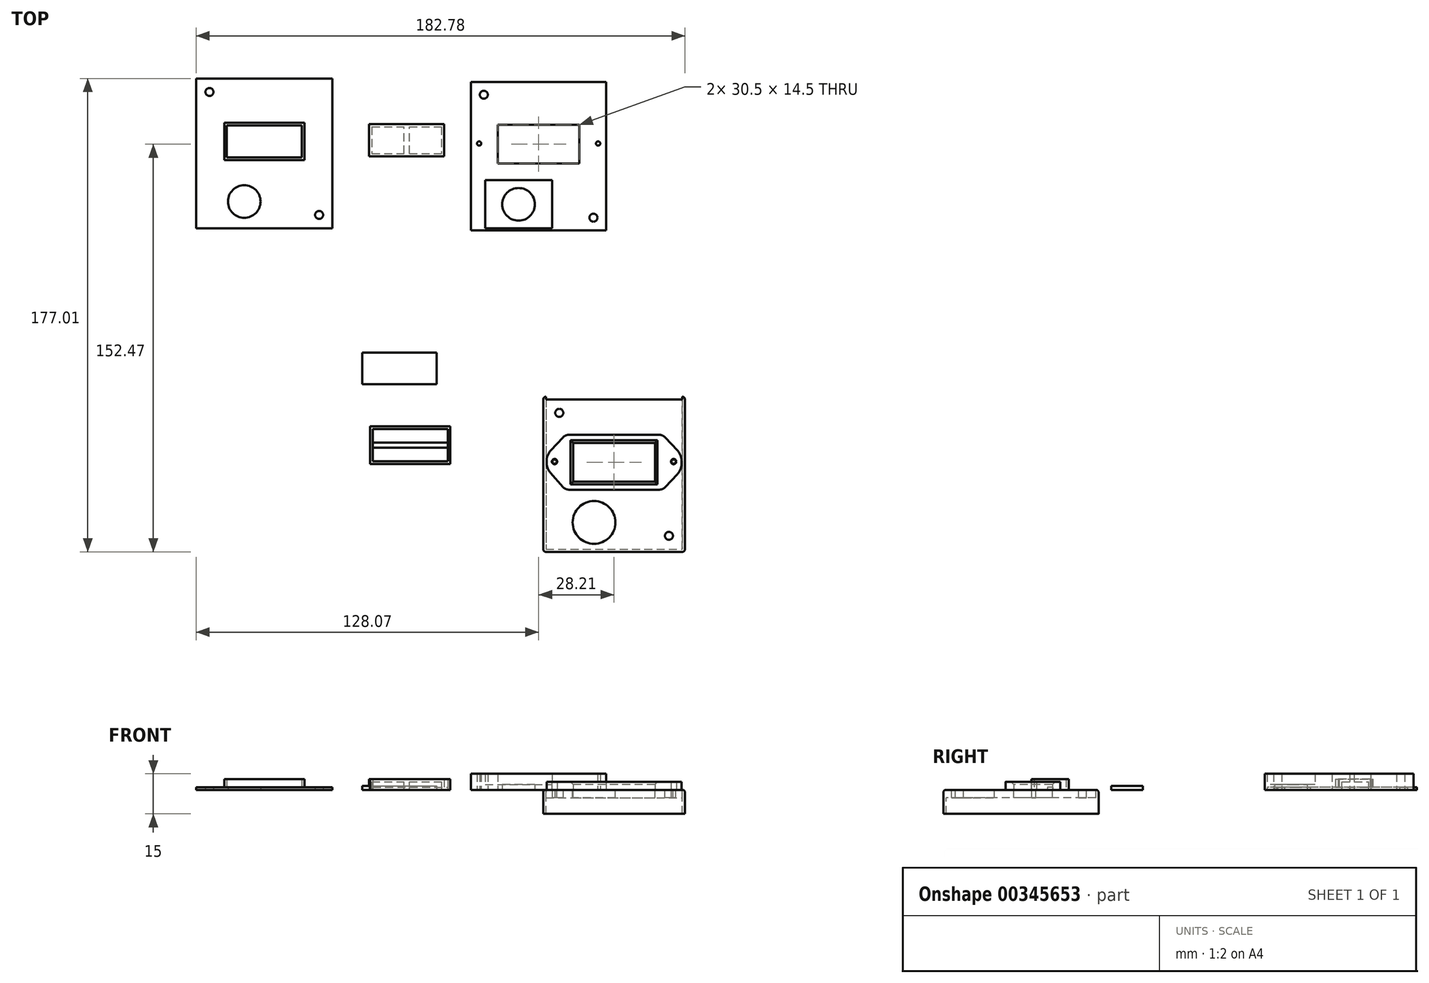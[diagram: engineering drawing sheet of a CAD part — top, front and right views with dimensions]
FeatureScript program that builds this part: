
annotation { "Feature Type Name" : "Feature", "Feature Type Description" : "" }
export const myFeature = defineFeature(function(context is Context, id is Id, definition is map)
    precondition{}
    {
        {
            var Q0;
            Q0=qCreatedBy(makeId("Top.planeOp"),FACE);
            var sketch = newSketch(context, id + "F0", { "sketchPlane" : qUnion([Q0])});
            skLineSegment(sketch, "E0.bottom", {"start": v(25.5, 28) * mm, "end": v(-25.5, 28) * mm});
            skLineSegment(sketch, "E0.top", {"start": v(25.5, -28) * mm, "end": v(-25.5, -28) * mm});
            skLineSegment(sketch, "E0.left", {"start": v(25.5, 28) * mm, "end": v(25.5, -28) * mm});
            skLineSegment(sketch, "E0.right", {"start": v(-25.5, 28) * mm, "end": v(-25.5, -28) * mm});
            skCircle(sketch, "E1", {"center": v(-20.5, 23) * mm, "radius": 1.5 * mm});
            skCircle(sketch, "E2", {"center": v(20.5, -23) * mm, "radius": 1.5 * mm});
            skCircle(sketch, "E3", {"center": v(-7.5, -18) * mm, "radius": 6.1 * mm});
            skLineSegment(sketch, "E4.bottom", {"start": v(-15.25, 11.75) * mm, "end": v(15.25, 11.75) * mm});
            skLineSegment(sketch, "E4.top", {"start": v(-15.25, -2.75) * mm, "end": v(15.25, -2.75) * mm});
            skLineSegment(sketch, "E4.left", {"start": v(-15.25, 11.75) * mm, "end": v(-15.25, -2.75) * mm});
            skLineSegment(sketch, "E4.right", {"start": v(15.25, 11.75) * mm, "end": v(15.25, -2.75) * mm});
            skPoint(sketch, "E5.middle", {"position": v(-103.8, -4.8) * mm});
            skLineSegment(sketch, "E6.bottom", {"start": v(-116.57, 11.54) * mm, "end": v(-88.57, 11.54) * mm});
            skLineSegment(sketch, "E6.top", {"start": v(-116.57, -0.46) * mm, "end": v(-88.57, -0.46) * mm});
            skLineSegment(sketch, "E6.left", {"start": v(-116.57, 11.54) * mm, "end": v(-116.57, -0.46) * mm});
            skLineSegment(sketch, "E6.right", {"start": v(-88.57, 11.54) * mm, "end": v(-88.57, -0.46) * mm});
            skLineSegment(sketch, "E7.bottom", {"start": v(-112.82, 11.54) * mm, "end": v(-110.32, 11.54) * mm});
            skLineSegment(sketch, "E7.top", {"start": v(-112.82, -0.46) * mm, "end": v(-110.32, -0.46) * mm});
            skLineSegment(sketch, "E7.left", {"start": v(-112.82, 11.54) * mm, "end": v(-112.82, -0.46) * mm});
            skLineSegment(sketch, "E7.right", {"start": v(-110.32, 11.54) * mm, "end": v(-110.32, -0.46) * mm});
            skLineSegment(sketch, "E8.bottom", {"start": v(-94.82, 11.54) * mm, "end": v(-92.32, 11.54) * mm});
            skLineSegment(sketch, "E8.top", {"start": v(-94.82, -0.46) * mm, "end": v(-92.32, -0.46) * mm});
            skLineSegment(sketch, "E8.left", {"start": v(-94.82, 11.54) * mm, "end": v(-94.82, -0.46) * mm});
            skLineSegment(sketch, "E8.right", {"start": v(-92.32, 11.54) * mm, "end": v(-92.32, -0.46) * mm});
            skLineSegment(sketch, "E9.bottom", {"start": v(-114.57, 8.54) * mm, "end": v(-108.57, 8.54) * mm, "construction": true});
            skLineSegment(sketch, "E9.top", {"start": v(-114.57, 2.54) * mm, "end": v(-108.57, 2.54) * mm, "construction": true});
            skLineSegment(sketch, "E9.left", {"start": v(-114.57, 8.54) * mm, "end": v(-114.57, 2.54) * mm, "construction": true});
            skLineSegment(sketch, "E9.right", {"start": v(-108.57, 8.54) * mm, "end": v(-108.57, 2.54) * mm, "construction": true});
            skLineSegment(sketch, "E10.bottom", {"start": v(-96.57, 8.54) * mm, "end": v(-90.57, 8.54) * mm, "construction": true});
            skLineSegment(sketch, "E10.top", {"start": v(-96.57, 2.54) * mm, "end": v(-90.57, 2.54) * mm, "construction": true});
            skLineSegment(sketch, "E10.left", {"start": v(-96.57, 8.54) * mm, "end": v(-96.57, 2.54) * mm, "construction": true});
            skLineSegment(sketch, "E10.right", {"start": v(-90.57, 8.54) * mm, "end": v(-90.57, 2.54) * mm, "construction": true});
            skLineSegment(sketch, "E11.bottom", {"start": v(-2.5, 11.75) * mm, "end": v(2.5, 11.75) * mm});
            skLineSegment(sketch, "E11.top", {"start": v(-2.5, -2.75) * mm, "end": v(2.5, -2.75) * mm});
            skLineSegment(sketch, "E11.left", {"start": v(-2.5, 11.75) * mm, "end": v(-2.5, -2.75) * mm});
            skLineSegment(sketch, "E11.right", {"start": v(2.5, 11.75) * mm, "end": v(2.5, -2.75) * mm});
            skLineSegment(sketch, "E12.bottom", {"start": v(-6.25, 10.5) * mm, "end": v(5.75, 10.5) * mm, "construction": true});
            skLineSegment(sketch, "E12.top", {"start": v(-6.25, -1.5) * mm, "end": v(5.75, -1.5) * mm, "construction": true});
            skLineSegment(sketch, "E12.left", {"start": v(-6.25, 10.5) * mm, "end": v(-6.25, -1.5) * mm, "construction": true});
            skLineSegment(sketch, "E12.right", {"start": v(5.75, 10.5) * mm, "end": v(5.75, -1.5) * mm, "construction": true});
            skLineSegment(sketch, "E13.bottom", {"start": v(-128.07, 29.04) * mm, "end": v(-77.07, 29.04) * mm});
            skLineSegment(sketch, "E13.top", {"start": v(-128.07, -26.96) * mm, "end": v(-77.07, -26.96) * mm});
            skLineSegment(sketch, "E13.left", {"start": v(-128.07, 29.04) * mm, "end": v(-128.07, -26.96) * mm});
            skLineSegment(sketch, "E13.right", {"start": v(-77.07, 29.04) * mm, "end": v(-77.07, -26.96) * mm});
            skCircle(sketch, "E14", {"center": v(-123.07, 24.04) * mm, "radius": 1.5 * mm});
            skCircle(sketch, "E15", {"center": v(-82.07, -21.96) * mm, "radius": 1.5 * mm});
            skLineSegment(sketch, "E16.bottom", {"start": v(-14, 10.5) * mm, "end": v(14, 10.5) * mm, "construction": true});
            skLineSegment(sketch, "E16.top", {"start": v(-14, -1.5) * mm, "end": v(14, -1.5) * mm, "construction": true});
            skLineSegment(sketch, "E16.left", {"start": v(-14, 10.5) * mm, "end": v(-14, -1.5) * mm, "construction": true});
            skLineSegment(sketch, "E16.right", {"start": v(14, 10.5) * mm, "end": v(14, -1.5) * mm, "construction": true});
            skCircle(sketch, "E17", {"center": v(-110.07, -16.96) * mm, "radius": 6.1 * mm});
            skSolve(sketch);
        }
        {
            var Q0;
            Q0=makeQuery(id+"F0.imprint","IMPRINT",FACE,{"disambiguationData":[TD([[makeQuery(id+"F0.imprint","IMPRINT",EDGE,{"derivedFrom":sQuery(id+"F0.wireOp",EDGE,"E0.bottom")}),1.0]])]});
            var Q1;
            Q1=makeQuery(id+"F0.imprint","IMPRINT",FACE,{"disambiguationData":[TD([[makeQuery(id+"F0.imprint","IMPRINT",EDGE,{"derivedFrom":sQuery(id+"F0.wireOp",EDGE,"LN2d2Qam-zQ4N-hJWI-jsZm-hQ2YjQqxJFMe.bottom")}),-1.0]])]});
            var Q2;
            Q2=makeQuery(id+"F0.imprint","IMPRINT",FACE,{"disambiguationData":[TD([[makeQuery(id+"F0.imprint","IMPRINT",EDGE,{"derivedFrom":sQuery(id+"F0.wireOp",EDGE,"Tyq8l7xN-NJ6r-rAiC-5Q4v-MCzvgNdMf9WX.bottom")}),-1.0]])]});
            var Q3;
            Q3=makeQuery(id+"F0.imprint","IMPRINT",FACE,{"disambiguationData":[TD([[makeQuery(id+"F0.imprint","IMPRINT",EDGE,{"derivedFrom":sQuery(id+"F0.wireOp",EDGE,"E11.bottom")}),-1.0]])]});
            var Q4;
            {var subQ12=sQuery(id+"F0.wireOp",EDGE,"E6.left");Q4=makeQuery(id+"F0.imprint","IMPRINT",FACE,{"disambiguationData":[TD([[makeQuery(id+"F0.imprint","IMPRINT",EDGE,{"derivedFrom":subQ12}),-1.0]])]});}
            var Q5;
            Q5=makeQuery(id+"F0.imprint","IMPRINT",FACE,{"disambiguationData":[TD([[makeQuery(id+"F0.imprint","IMPRINT",EDGE,{"derivedFrom":sQuery(id+"F0.wireOp",EDGE,"E7.bottom")}),-1.0]])]});
            var Q6;
            Q6=makeQuery(id+"F0.imprint","IMPRINT",FACE,{"disambiguationData":[TD([[makeQuery(id+"F0.imprint","IMPRINT",EDGE,{"derivedFrom":sQuery(id+"F0.wireOp",EDGE,"E8.bottom")}),-1.0]])]});
            var Q7;
            Q7=makeQuery(id+"F0.imprint","IMPRINT",FACE,{"disambiguationData":[TD([[makeQuery(id+"F0.imprint","IMPRINT",EDGE,{"derivedFrom":sQuery(id+"F0.wireOp",EDGE,"V3zyF6Pa-9TGi-MSfi-dUwD-Oto6uP0OLka4.bottom")}),-1.0]])]});
            extrude(context, id + "F1", {"entities" : qUnion([Q0, Q1, Q2, Q3, Q4, Q5, Q6, Q7]), "depth" : 1 * mm});
        }
        {
            var Q0;
            Q0=qCreatedBy(makeId("Top.planeOp"),FACE);
            var sketch = newSketch(context, id + "F2", { "sketchPlane" : qUnion([Q0])});
            skPoint(sketch, "E18.middle", {"position": v(28.78, -122.02) * mm});
            skLineSegment(sketch, "E19.bottom", {"start": v(14.21, -108.47) * mm, "end": v(42.21, -108.47) * mm, "construction": true});
            skLineSegment(sketch, "E19.top", {"start": v(14.21, -120.47) * mm, "end": v(42.21, -120.47) * mm, "construction": true});
            skLineSegment(sketch, "E19.left", {"start": v(14.21, -108.47) * mm, "end": v(14.21, -120.47) * mm, "construction": true});
            skLineSegment(sketch, "E19.right", {"start": v(42.21, -108.47) * mm, "end": v(42.21, -120.47) * mm, "construction": true});
            skLineSegment(sketch, "E20.bottom", {"start": v(20.96, -108.47) * mm, "end": v(23.46, -108.47) * mm, "construction": true});
            skLineSegment(sketch, "E20.top", {"start": v(20.96, -120.47) * mm, "end": v(23.46, -120.47) * mm, "construction": true});
            skLineSegment(sketch, "E20.left", {"start": v(20.96, -108.47) * mm, "end": v(20.96, -120.47) * mm, "construction": true});
            skLineSegment(sketch, "E20.right", {"start": v(23.46, -108.47) * mm, "end": v(23.46, -120.47) * mm, "construction": true});
            skLineSegment(sketch, "E21.bottom", {"start": v(32.96, -108.47) * mm, "end": v(35.46, -108.47) * mm, "construction": true});
            skLineSegment(sketch, "E21.top", {"start": v(32.96, -120.47) * mm, "end": v(35.46, -120.47) * mm, "construction": true});
            skLineSegment(sketch, "E21.left", {"start": v(32.96, -108.47) * mm, "end": v(32.96, -120.47) * mm, "construction": true});
            skLineSegment(sketch, "E21.right", {"start": v(35.46, -108.47) * mm, "end": v(35.46, -120.47) * mm, "construction": true});
            skLineSegment(sketch, "E22.bottom", {"start": v(19.21, -111.47) * mm, "end": v(25.21, -111.47) * mm, "construction": true});
            skLineSegment(sketch, "E22.top", {"start": v(19.21, -117.47) * mm, "end": v(25.21, -117.47) * mm, "construction": true});
            skLineSegment(sketch, "E22.left", {"start": v(19.21, -111.47) * mm, "end": v(19.21, -117.47) * mm, "construction": true});
            skLineSegment(sketch, "E22.right", {"start": v(25.21, -111.47) * mm, "end": v(25.21, -117.47) * mm, "construction": true});
            skLineSegment(sketch, "E23.bottom", {"start": v(31.21, -111.47) * mm, "end": v(37.21, -111.47) * mm, "construction": true});
            skLineSegment(sketch, "E23.top", {"start": v(31.21, -117.47) * mm, "end": v(37.21, -117.47) * mm, "construction": true});
            skLineSegment(sketch, "E23.left", {"start": v(31.21, -111.47) * mm, "end": v(31.21, -117.47) * mm, "construction": true});
            skLineSegment(sketch, "E23.right", {"start": v(37.21, -111.47) * mm, "end": v(37.21, -117.47) * mm, "construction": true});
            skLineSegment(sketch, "E24.bottom", {"start": v(2.71, -90.97) * mm, "end": v(53.71, -90.97) * mm});
            skLineSegment(sketch, "E24.top", {"start": v(2.71, -146.97) * mm, "end": v(53.71, -146.97) * mm});
            skLineSegment(sketch, "E24.left", {"start": v(2.71, -90.97) * mm, "end": v(2.71, -146.97) * mm});
            skLineSegment(sketch, "E24.right", {"start": v(53.71, -90.97) * mm, "end": v(53.71, -146.97) * mm});
            skCircle(sketch, "E25", {"center": v(7.71, -95.97) * mm, "radius": 1.5 * mm});
            skCircle(sketch, "E26", {"center": v(48.71, -141.97) * mm, "radius": 1.5 * mm});
            skCircle(sketch, "E27", {"center": v(20.71, -136.97) * mm, "radius": 8 * mm});
            skLineSegment(sketch, "E28.bottom", {"start": v(12.96, -107.22) * mm, "end": v(43.46, -107.22) * mm});
            skLineSegment(sketch, "E28.top", {"start": v(12.96, -121.72) * mm, "end": v(43.46, -121.72) * mm});
            skLineSegment(sketch, "E28.left", {"start": v(12.96, -107.22) * mm, "end": v(12.96, -121.72) * mm});
            skLineSegment(sketch, "E28.right", {"start": v(43.46, -107.22) * mm, "end": v(43.46, -121.72) * mm});
            skPoint(sketch, "E29.middle", {"position": v(-49.22, -118.43) * mm});
            skLineSegment(sketch, "E30.bottom", {"start": v(-62, -102.08) * mm, "end": v(-34, -102.08) * mm});
            skLineSegment(sketch, "E30.top", {"start": v(-62, -114.08) * mm, "end": v(-34, -114.08) * mm});
            skLineSegment(sketch, "E30.left", {"start": v(-62, -102.08) * mm, "end": v(-62, -114.08) * mm});
            skLineSegment(sketch, "E30.right", {"start": v(-34, -102.08) * mm, "end": v(-34, -114.08) * mm});
            skLineSegment(sketch, "E31.bottom", {"start": v(-57.25, -102.08) * mm, "end": v(-54.75, -102.08) * mm, "construction": true});
            skLineSegment(sketch, "E31.top", {"start": v(-57.25, -114.08) * mm, "end": v(-54.75, -114.08) * mm, "construction": true});
            skLineSegment(sketch, "E31.left", {"start": v(-57.25, -102.08) * mm, "end": v(-57.25, -114.08) * mm, "construction": true});
            skLineSegment(sketch, "E31.right", {"start": v(-54.75, -102.08) * mm, "end": v(-54.75, -114.08) * mm, "construction": true});
            skLineSegment(sketch, "E32.bottom", {"start": v(-41.25, -102.08) * mm, "end": v(-38.75, -102.08) * mm, "construction": true});
            skLineSegment(sketch, "E32.top", {"start": v(-41.25, -114.08) * mm, "end": v(-38.75, -114.08) * mm, "construction": true});
            skLineSegment(sketch, "E32.left", {"start": v(-41.25, -102.08) * mm, "end": v(-41.25, -114.08) * mm, "construction": true});
            skLineSegment(sketch, "E32.right", {"start": v(-38.75, -102.08) * mm, "end": v(-38.75, -114.08) * mm, "construction": true});
            skLineSegment(sketch, "E33.bottom", {"start": v(-59, -105.08) * mm, "end": v(-53, -105.08) * mm, "construction": true});
            skLineSegment(sketch, "E33.top", {"start": v(-59, -111.08) * mm, "end": v(-53, -111.08) * mm, "construction": true});
            skLineSegment(sketch, "E33.left", {"start": v(-59, -105.08) * mm, "end": v(-59, -111.08) * mm, "construction": true});
            skLineSegment(sketch, "E33.right", {"start": v(-53, -105.08) * mm, "end": v(-53, -111.08) * mm, "construction": true});
            skLineSegment(sketch, "E34.bottom", {"start": v(-43, -105.08) * mm, "end": v(-37, -105.08) * mm, "construction": true});
            skLineSegment(sketch, "E34.top", {"start": v(-43, -111.08) * mm, "end": v(-37, -111.08) * mm, "construction": true});
            skLineSegment(sketch, "E34.left", {"start": v(-43, -105.08) * mm, "end": v(-43, -111.08) * mm, "construction": true});
            skLineSegment(sketch, "E34.right", {"start": v(-37, -105.08) * mm, "end": v(-37, -111.08) * mm, "construction": true});
            skLineSegment(sketch, "E35.bottom", {"start": v(-63, -101.08) * mm, "end": v(-33, -101.08) * mm});
            skLineSegment(sketch, "E35.top", {"start": v(-63, -115.08) * mm, "end": v(-33, -115.08) * mm});
            skLineSegment(sketch, "E35.left", {"start": v(-63, -101.08) * mm, "end": v(-63, -115.08) * mm});
            skLineSegment(sketch, "E35.right", {"start": v(-33, -101.08) * mm, "end": v(-33, -115.08) * mm});
            skLineSegment(sketch, "E36.bottom", {"start": v(-62, -107.08) * mm, "end": v(-34, -107.08) * mm});
            skLineSegment(sketch, "E36.top", {"start": v(-62, -109.08) * mm, "end": v(-34, -109.08) * mm});
            skLineSegment(sketch, "E36.left", {"start": v(-62, -107.08) * mm, "end": v(-62, -109.08) * mm});
            skLineSegment(sketch, "E36.right", {"start": v(-34, -107.08) * mm, "end": v(-34, -109.08) * mm});
            skLineSegment(sketch, "E37.bottom", {"start": v(-53, -102.08) * mm, "end": v(-43, -102.08) * mm});
            skLineSegment(sketch, "E37.top", {"start": v(-53, -114.08) * mm, "end": v(-43, -114.08) * mm});
            skLineSegment(sketch, "E37.left", {"start": v(-53, -102.08) * mm, "end": v(-53, -114.08) * mm});
            skLineSegment(sketch, "E37.right", {"start": v(-43, -102.08) * mm, "end": v(-43, -114.08) * mm});
            skLineSegment(sketch, "E38.top", {"start": v(2.71, -89.97) * mm, "end": v(53.71, -89.97) * mm});
            skLineSegment(sketch, "E38.left", {"start": v(2.71, -90.97) * mm, "end": v(2.71, -89.97) * mm});
            skLineSegment(sketch, "E38.right", {"start": v(53.71, -90.97) * mm, "end": v(53.71, -89.97) * mm});
            skLineSegment(sketch, "E39.top", {"start": v(2.71, -147.97) * mm, "end": v(53.71, -147.97) * mm});
            skLineSegment(sketch, "E39.left", {"start": v(2.71, -146.97) * mm, "end": v(2.71, -147.97) * mm});
            skLineSegment(sketch, "E39.right", {"start": v(53.71, -146.97) * mm, "end": v(53.71, -147.97) * mm});
            skLineSegment(sketch, "E40.bottom", {"start": v(53.71, -89.97) * mm, "end": v(54.71, -89.97) * mm});
            skLineSegment(sketch, "E40.top", {"start": v(53.71, -147.97) * mm, "end": v(54.71, -147.97) * mm});
            skLineSegment(sketch, "E40.left", {"start": v(53.71, -89.97) * mm, "end": v(53.71, -147.97) * mm});
            skLineSegment(sketch, "E40.right", {"start": v(54.71, -89.97) * mm, "end": v(54.71, -147.97) * mm});
            skLineSegment(sketch, "E41.bottom", {"start": v(2.71, -89.97) * mm, "end": v(1.71, -89.97) * mm});
            skLineSegment(sketch, "E41.top", {"start": v(2.71, -147.97) * mm, "end": v(1.71, -147.97) * mm});
            skLineSegment(sketch, "E41.left", {"start": v(2.71, -89.97) * mm, "end": v(2.71, -147.97) * mm});
            skLineSegment(sketch, "E41.right", {"start": v(1.71, -89.97) * mm, "end": v(1.71, -147.97) * mm});
            skCircle(sketch, "E42", {"center": v(5.96, -114.22) * mm, "radius": 0.8 * mm});
            skCircle(sketch, "E43", {"center": v(50.46, -114.22) * mm, "radius": 0.8 * mm});
            skSolve(sketch);
        }
        {
            var Q0;
            Q0=makeQuery(id+"F1.opExtrude","CAP_FACE",FACE,{"disambiguationData":[OSD([sQuery(id+"F0.wireOp",EDGE,"E6.bottom"),sQuery(id+"F0.wireOp",EDGE,"E6.top"),sQuery(id+"F0.wireOp",EDGE,"E6.left"),sQuery(id+"F0.wireOp",EDGE,"E6.right"),sQuery(id+"F0.wireOp",EDGE,"E7.left"),sQuery(id+"F0.wireOp",EDGE,"E7.right"),sQuery(id+"F0.wireOp",EDGE,"E8.left"),sQuery(id+"F0.wireOp",EDGE,"E8.right"),sQuery(id+"F0.wireOp",EDGE,"E13.bottom"),sQuery(id+"F0.wireOp",EDGE,"E13.top"),sQuery(id+"F0.wireOp",EDGE,"E13.left"),sQuery(id+"F0.wireOp",EDGE,"E13.right"),sQuery(id+"F0.wireOp",EDGE,"E14"),sQuery(id+"F0.wireOp",EDGE,"E15"),sQuery(id+"F0.wireOp",EDGE,"E17"),sQuery(id+"F0.wireOp",EDGE,"V3zyF6Pa-9TGi-MSfi-dUwD-Oto6uP0OLka4.left"),sQuery(id+"F0.wireOp",EDGE,"V3zyF6Pa-9TGi-MSfi-dUwD-Oto6uP0OLka4.right")])],"isStart":false});
            var sketch = newSketch(context, id + "F3", { "sketchPlane" : qUnion([Q0])});
            skLineSegment(sketch, "E44.bottom", {"start": v(-116.57, 11.54) * mm, "end": v(-88.57, 11.54) * mm});
            skLineSegment(sketch, "E44.top", {"start": v(-116.57, 12.54) * mm, "end": v(-88.57, 12.54) * mm});
            skLineSegment(sketch, "E44.left", {"start": v(-116.57, 11.54) * mm, "end": v(-116.57, 12.54) * mm});
            skLineSegment(sketch, "E44.right", {"start": v(-88.57, 11.54) * mm, "end": v(-88.57, 12.54) * mm});
            skLineSegment(sketch, "E45.bottom", {"start": v(-116.57, -0.46) * mm, "end": v(-88.57, -0.46) * mm});
            skLineSegment(sketch, "E45.top", {"start": v(-116.57, -1.46) * mm, "end": v(-88.57, -1.46) * mm});
            skLineSegment(sketch, "E45.left", {"start": v(-116.57, -0.46) * mm, "end": v(-116.57, -1.46) * mm});
            skLineSegment(sketch, "E45.right", {"start": v(-88.57, -0.46) * mm, "end": v(-88.57, -1.46) * mm});
            skLineSegment(sketch, "E46.bottom", {"start": v(-116.57, -1.46) * mm, "end": v(-117.57, -1.46) * mm});
            skLineSegment(sketch, "E46.top", {"start": v(-116.57, 12.54) * mm, "end": v(-117.57, 12.54) * mm});
            skLineSegment(sketch, "E46.left", {"start": v(-116.57, -1.46) * mm, "end": v(-116.57, 12.54) * mm});
            skLineSegment(sketch, "E46.right", {"start": v(-117.57, -1.46) * mm, "end": v(-117.57, 12.54) * mm});
            skLineSegment(sketch, "E47.bottom", {"start": v(-88.57, 12.54) * mm, "end": v(-87.57, 12.54) * mm});
            skLineSegment(sketch, "E47.top", {"start": v(-88.57, -1.46) * mm, "end": v(-87.57, -1.46) * mm});
            skLineSegment(sketch, "E47.left", {"start": v(-88.57, 12.54) * mm, "end": v(-88.57, -1.46) * mm});
            skLineSegment(sketch, "E47.right", {"start": v(-87.57, 12.54) * mm, "end": v(-87.57, -1.46) * mm});
            skSolve(sketch);
        }
        {
            var Q0;
            Q0 = qSketchRegion(id + "F3", true);
            extrude(context, id + "F4", {"entities" : qUnion([Q0]), "operationType" : NewBodyOperationType.ADD, "depth" : 3 * mm});
        }
        {
            var Q0;
            Q0=qCreatedBy(makeId("Top.planeOp"),FACE);
            var sketch = newSketch(context, id + "F5", { "sketchPlane" : qUnion([Q0])});
            skLineSegment(sketch, "E48.bottom", {"start": v(-63.36, 12) * mm, "end": v(-35.36, 12) * mm});
            skLineSegment(sketch, "E48.top", {"start": v(-63.36, 0) * mm, "end": v(-35.36, 0) * mm});
            skLineSegment(sketch, "E48.left", {"start": v(-63.36, 12) * mm, "end": v(-63.36, 0) * mm});
            skLineSegment(sketch, "E48.right", {"start": v(-35.36, 12) * mm, "end": v(-35.36, 0) * mm});
            skLineSegment(sketch, "E49.bottom", {"start": v(-65.94, -73.47) * mm, "end": v(-38.14, -73.47) * mm});
            skLineSegment(sketch, "E49.top", {"start": v(-65.94, -85.27) * mm, "end": v(-38.14, -85.27) * mm});
            skLineSegment(sketch, "E49.left", {"start": v(-65.94, -73.47) * mm, "end": v(-65.94, -85.27) * mm});
            skLineSegment(sketch, "E49.right", {"start": v(-38.14, -73.47) * mm, "end": v(-38.14, -85.27) * mm});
            skSolve(sketch);
        }
        {
            var Q0;
            Q0=makeQuery(id+"F5.imprint","IMPRINT",FACE,{"disambiguationData":[TD([[makeQuery(id+"F5.imprint","IMPRINT",EDGE,{"derivedFrom":sQuery(id+"F5.wireOp",EDGE,"E48.bottom")}),-1.0]])]});
            extrude(context, id + "F6", {"entities" : qUnion([Q0]), "depth" : 4 * mm});
        }
        {
            var Q0;
            Q0=makeQuery(id+"F6.opExtrude","CAP_FACE",FACE,{"disambiguationData":[OSD([sQuery(id+"F5.wireOp",EDGE,"E48.bottom"),sQuery(id+"F5.wireOp",EDGE,"E48.top"),sQuery(id+"F5.wireOp",EDGE,"E48.left"),sQuery(id+"F5.wireOp",EDGE,"E48.right")])],"isStart":true});
            shell(context, id + "F7", {"entities" : qUnion([Q0]), "thickness" : 1 * mm});
        }
        {
            var Q0;
            Q0=makeQuery(id+"F7.opShell","OFFSET_FACE",FACE,{"disambiguationData":[OSD([sQuery(id+"F5.wireOp",EDGE,"E48.bottom"),sQuery(id+"F5.wireOp",EDGE,"E48.top"),sQuery(id+"F5.wireOp",EDGE,"E48.left"),sQuery(id+"F5.wireOp",EDGE,"E48.right")])]});
            var sketch = newSketch(context, id + "F8", { "sketchPlane" : qUnion([Q0])});
            skLineSegment(sketch, "E50.bottom", {"start": v(-50.36, -1) * mm, "end": v(-48.36, -1) * mm});
            skLineSegment(sketch, "E50.top", {"start": v(-50.36, -11) * mm, "end": v(-48.36, -11) * mm});
            skLineSegment(sketch, "E50.left", {"start": v(-50.36, -1) * mm, "end": v(-50.36, -11) * mm});
            skLineSegment(sketch, "E50.right", {"start": v(-48.36, -1) * mm, "end": v(-48.36, -11) * mm});
            skSolve(sketch);
        }
        {
            var Q0;
            Q0=makeQuery(id+"F8.imprint","IMPRINT",FACE,{"disambiguationData":[TD([[makeQuery(id+"F8.imprint","IMPRINT",EDGE,{"derivedFrom":sQuery(id+"F8.wireOp",EDGE,"E50.bottom")}),-1.0]])]});
            extrude(context, id + "F9", {"entities" : qUnion([Q0]), "operationType" : NewBodyOperationType.ADD, "depth" : 3 * mm});
        }
        {
            var Q0;
            Q0=makeQuery(id+"F1.opExtrude","CAP_FACE",FACE,{"disambiguationData":[OSD([sQuery(id+"F0.wireOp",EDGE,"E0.bottom"),sQuery(id+"F0.wireOp",EDGE,"E0.top"),sQuery(id+"F0.wireOp",EDGE,"E0.left"),sQuery(id+"F0.wireOp",EDGE,"E0.right"),sQuery(id+"F0.wireOp",EDGE,"E1"),sQuery(id+"F0.wireOp",EDGE,"E2"),sQuery(id+"F0.wireOp",EDGE,"E3"),sQuery(id+"F0.wireOp",EDGE,"E4.bottom"),sQuery(id+"F0.wireOp",EDGE,"E4.top"),sQuery(id+"F0.wireOp",EDGE,"E4.left"),sQuery(id+"F0.wireOp",EDGE,"E4.right"),sQuery(id+"F0.wireOp",EDGE,"E11.left"),sQuery(id+"F0.wireOp",EDGE,"E11.right")])],"isStart":false});
            var sketch = newSketch(context, id + "F10", { "sketchPlane" : qUnion([Q0])});
            skLineSegment(sketch, "E51.bottom", {"start": v(-6.25, 10.25) * mm, "end": v(5.75, 10.25) * mm, "construction": true});
            skLineSegment(sketch, "E51.top", {"start": v(-6.25, -1.75) * mm, "end": v(5.75, -1.75) * mm, "construction": true});
            skLineSegment(sketch, "E51.left", {"start": v(-6.25, 10.25) * mm, "end": v(-6.25, -1.75) * mm, "construction": true});
            skLineSegment(sketch, "E51.right", {"start": v(5.75, 10.25) * mm, "end": v(5.75, -1.75) * mm, "construction": true});
            skSolve(sketch);
        }
        {
            var Q0;
            {var subQ3=sQuery(id+"F2.wireOp",EDGE,"E30.left");Q0=makeQuery(id+"F2.imprint","IMPRINT",FACE,{"disambiguationData":[TD([[makeQuery(id+"F2.imprint","IMPRINT",EDGE,{"derivedFrom":subQ3}),-1.0]])]});}
            extrude(context, id + "F11", {"entities" : qUnion([Q0]), "depth" : 4 * mm});
        }
        {
            var Q0;
            Q0=makeQuery(id+"F2.imprint","IMPRINT",FACE,{"disambiguationData":[TD([[makeQuery(id+"F2.imprint","IMPRINT",EDGE,{"derivedFrom":sQuery(id+"F2.wireOp",EDGE,"E25")}),-1.0]])]});
            extrude(context, id + "F12", {"entities" : qUnion([Q0]), "oppositeDirection" : true, "depth" : 3 * mm});
        }
        {
            var Q0;
            Q0=makeQuery(id+"F2.imprint","IMPRINT",FACE,{"disambiguationData":[TD([[makeQuery(id+"F2.imprint","IMPRINT",EDGE,{"derivedFrom":sQuery(id+"F2.wireOp",EDGE,"E36.bottom")}),-1.0]])]});
            var Q1;
            {var subQ5=sQuery(id+"F2.wireOp",EDGE,"E37.bottom");Q1=makeQuery(id+"F2.imprint","IMPRINT",FACE,{"disambiguationData":[TD([[makeQuery(id+"F2.imprint","IMPRINT",EDGE,{"derivedFrom":subQ5}),-1.0]])]});}
            var Q2;
            {var subQ5=sQuery(id+"F2.wireOp",EDGE,"E37.top");Q2=makeQuery(id+"F2.imprint","IMPRINT",FACE,{"disambiguationData":[TD([[makeQuery(id+"F2.imprint","IMPRINT",EDGE,{"derivedFrom":subQ5}),1.0]])]});}
            extrude(context, id + "F13", {"entities" : qUnion([Q0, Q1, Q2]), "operationType" : NewBodyOperationType.ADD, "depth" : 1 * mm});
        }
        {
            var Q0;
            Q0=makeQuery(id+"F5.imprint","IMPRINT",FACE,{"disambiguationData":[TD([[makeQuery(id+"F5.imprint","IMPRINT",EDGE,{"derivedFrom":sQuery(id+"F5.wireOp",EDGE,"E49.bottom")}),-1.0]])]});
            extrude(context, id + "F14", {"entities" : qUnion([Q0]), "depth" : 1.5 * mm});
        }
        {
            var Q0;
            {var subQ3=sQuery(id+"F2.wireOp",EDGE,"E41.bottom");Q0=makeQuery(id+"F2.imprint","IMPRINT",FACE,{"disambiguationData":[TD([[makeQuery(id+"F2.imprint","IMPRINT",EDGE,{"derivedFrom":subQ3}),1.0]])]});}
            var Q1;
            {var subQ0=sQuery(id+"F2.wireOp",EDGE,"E24.bottom");Q1=makeQuery(id+"F2.imprint","IMPRINT",FACE,{"disambiguationData":[TD([[makeQuery(id+"F2.imprint","IMPRINT",EDGE,{"derivedFrom":subQ0}),1.0]])]});}
            var Q2;
            {var subQ0=sQuery(id+"F2.wireOp",EDGE,"E24.top");Q2=makeQuery(id+"F2.imprint","IMPRINT",FACE,{"disambiguationData":[TD([[makeQuery(id+"F2.imprint","IMPRINT",EDGE,{"derivedFrom":subQ0}),-1.0]])]});}
            var Q3;
            {var subQ3=sQuery(id+"F2.wireOp",EDGE,"E40.bottom");Q3=makeQuery(id+"F2.imprint","IMPRINT",FACE,{"disambiguationData":[TD([[makeQuery(id+"F2.imprint","IMPRINT",EDGE,{"derivedFrom":subQ3}),-1.0]])]});}
            extrude(context, id + "F15", {"entities" : qUnion([Q0, Q1, Q2, Q3]), "operationType" : NewBodyOperationType.ADD, "oppositeDirection" : true, "depth" : 9 * mm});
        }
        {
            var Q0;
            Q0=makeQuery(id+"F2.imprint","IMPRINT",FACE,{"disambiguationData":[TD([[makeQuery(id+"F2.imprint","IMPRINT",EDGE,{"derivedFrom":sQuery(id+"F2.wireOp",EDGE,"E25")}),-1.0]])]});
            var sketch = newSketch(context, id + "F16", { "sketchPlane" : qUnion([Q0])});
            skLineSegment(sketch, "E52.bottom", {"start": v(9.96, -104.22) * mm, "end": v(46.46, -104.22) * mm});
            skLineSegment(sketch, "E52.top", {"start": v(9.96, -124.72) * mm, "end": v(46.46, -124.72) * mm});
            skLineSegment(sketch, "E52.left", {"start": v(9.96, -104.22) * mm, "end": v(9.96, -124.72) * mm});
            skLineSegment(sketch, "E52.right", {"start": v(46.46, -104.22) * mm, "end": v(46.46, -124.72) * mm});
            skLineSegment(sketch, "E53", {"start": v(9.96, -124.72) * mm, "end": v(2.96, -116.72) * mm});
            skLineSegment(sketch, "E54", {"start": v(2.96, -116.72) * mm, "end": v(2.96, -111.72) * mm});
            skLineSegment(sketch, "E55", {"start": v(2.96, -111.72) * mm, "end": v(9.96, -104.22) * mm});
            skCircle(sketch, "E56", {"center": v(5.96, -114.22) * mm, "radius": 1 * mm});
            skLineSegment(sketch, "E57.bottom", {"start": v(12.96, -107.22) * mm, "end": v(43.46, -107.22) * mm});
            skLineSegment(sketch, "E57.top", {"start": v(12.96, -121.72) * mm, "end": v(43.46, -121.72) * mm});
            skLineSegment(sketch, "E57.left", {"start": v(12.96, -107.22) * mm, "end": v(12.96, -121.72) * mm});
            skLineSegment(sketch, "E57.right", {"start": v(43.46, -107.22) * mm, "end": v(43.46, -121.72) * mm});
            skLineSegment(sketch, "E58", {"start": v(46.46, -104.22) * mm, "end": v(53.46, -111.72) * mm});
            skLineSegment(sketch, "E59", {"start": v(53.46, -111.72) * mm, "end": v(53.46, -117.22) * mm});
            skLineSegment(sketch, "E60", {"start": v(53.46, -117.22) * mm, "end": v(46.46, -124.72) * mm});
            skCircle(sketch, "E61", {"center": v(50.46, -114.22) * mm, "radius": 1 * mm});
            skSolve(sketch);
        }
        {
            var Q0;
            Q0 = qSketchRegion(id + "F16", true);
            extrude(context, id + "F17", {"entities" : qUnion([Q0]), "depth" : 3 * mm});
        }
        {
            var Q0;
            Q0=makeQuery(id+"F17.opExtrude","SWEPT_EDGE",EDGE,{"disambiguationData":[OSD([sQuery(id+"F16.wireOp",EDGE,"E54"),sQuery(id+"F16.wireOp",EDGE,"E55")])]});
            var Q1;
            Q1=makeQuery(id+"F17.opExtrude","SWEPT_EDGE",EDGE,{"disambiguationData":[OSD([sQuery(id+"F16.wireOp",EDGE,"E53"),sQuery(id+"F16.wireOp",EDGE,"E54")])]});
            var Q2;
            Q2=makeQuery(id+"F17.opExtrude","SWEPT_EDGE",EDGE,{"disambiguationData":[OSD([sQuery(id+"F16.wireOp",EDGE,"E59"),sQuery(id+"F16.wireOp",EDGE,"E60")])]});
            var Q3;
            Q3=makeQuery(id+"F17.opExtrude","SWEPT_EDGE",EDGE,{"disambiguationData":[OSD([sQuery(id+"F16.wireOp",EDGE,"E58"),sQuery(id+"F16.wireOp",EDGE,"E59")])]});
            fillet(context, id + "F18", {"entities" : qUnion([Q0, Q1, Q2, Q3]), "radius" : 6 * mm, "tangentPropagation" : true, "allowEdgeOverflow" : false});
        }
        {
            var Q0;
            Q0=makeQuery(id+"F17.opExtrude","SWEPT_EDGE",EDGE,{"disambiguationData":[OSD([sQuery(id+"F16.wireOp",EDGE,"E52.bottom"),sQuery(id+"F16.wireOp",EDGE,"E52.left"),sQuery(id+"F16.wireOp",EDGE,"E55")])]});
            var Q1;
            Q1=makeQuery(id+"F17.opExtrude","SWEPT_EDGE",EDGE,{"disambiguationData":[OSD([sQuery(id+"F16.wireOp",EDGE,"E52.top"),sQuery(id+"F16.wireOp",EDGE,"E52.left"),sQuery(id+"F16.wireOp",EDGE,"E53")])]});
            var Q2;
            Q2=makeQuery(id+"F17.opExtrude","SWEPT_EDGE",EDGE,{"disambiguationData":[OSD([sQuery(id+"F16.wireOp",EDGE,"E52.top"),sQuery(id+"F16.wireOp",EDGE,"E52.right"),sQuery(id+"F16.wireOp",EDGE,"E60")])]});
            var Q3;
            Q3=makeQuery(id+"F17.opExtrude","SWEPT_EDGE",EDGE,{"disambiguationData":[OSD([sQuery(id+"F16.wireOp",EDGE,"E52.bottom"),sQuery(id+"F16.wireOp",EDGE,"E52.right"),sQuery(id+"F16.wireOp",EDGE,"E58")])]});
            fillet(context, id + "F19", {"entities" : qUnion([Q0, Q1, Q2, Q3]), "radius" : 3 * mm, "tangentPropagation" : true, "allowEdgeOverflow" : false});
        }
        {
            var Q0;
            Q0=makeQuery(id+"F15.opExtrude","CAP_EDGE",EDGE,{"disambiguationData":[OSD([sQuery(id+"F2.wireOp",EDGE,"E41.right")])],"isStart":true});
            var Q1;
            Q1=makeQuery(id+"F15.opExtrude","CAP_EDGE",EDGE,{"disambiguationData":[OSD([sQuery(id+"F2.wireOp",EDGE,"E38.top"),sQuery(id+"F2.wireOp",EDGE,"E40.bottom"),sQuery(id+"F2.wireOp",EDGE,"E41.bottom")])],"isStart":true});
            var Q2;
            Q2=makeQuery(id+"F15.opExtrude","CAP_EDGE",EDGE,{"disambiguationData":[OSD([sQuery(id+"F2.wireOp",EDGE,"E39.top"),sQuery(id+"F2.wireOp",EDGE,"E40.top"),sQuery(id+"F2.wireOp",EDGE,"E41.top")])],"isStart":true});
            var Q3;
            Q3=makeQuery(id+"F15.opExtrude","CAP_EDGE",EDGE,{"disambiguationData":[OSD([sQuery(id+"F2.wireOp",EDGE,"E40.right")])],"isStart":true});
            var Q4;
            Q4=makeQuery(id+"F15.opExtrude","SWEPT_EDGE",EDGE,{"disambiguationData":[OSD([sQuery(id+"F2.wireOp",EDGE,"E40.top"),sQuery(id+"F2.wireOp",EDGE,"E40.right")])]});
            var Q5;
            Q5=makeQuery(id+"F15.opExtrude","SWEPT_EDGE",EDGE,{"disambiguationData":[OSD([sQuery(id+"F2.wireOp",EDGE,"E41.top"),sQuery(id+"F2.wireOp",EDGE,"E41.right")])]});
            var Q6;
            Q6=makeQuery(id+"F15.opExtrude","SWEPT_EDGE",EDGE,{"disambiguationData":[OSD([sQuery(id+"F2.wireOp",EDGE,"E41.bottom"),sQuery(id+"F2.wireOp",EDGE,"E41.right")])]});
            var Q7;
            Q7=makeQuery(id+"F15.opExtrude","SWEPT_EDGE",EDGE,{"disambiguationData":[OSD([sQuery(id+"F2.wireOp",EDGE,"E40.bottom"),sQuery(id+"F2.wireOp",EDGE,"E40.right")])]});
            fillet(context, id + "F20", {"entities" : qUnion([Q0, Q1, Q2, Q3, Q4, Q5, Q6, Q7]), "radius" : 1 * mm, "tangentPropagation" : true, "allowEdgeOverflow" : false});
        }
        {
            var Q0;
            Q0=makeQuery(id+"F17.opExtrude","CAP_EDGE",EDGE,{"disambiguationData":[OSD([sQuery(id+"F16.wireOp",EDGE,"E57.left")])],"isStart":false});
            var Q1;
            Q1=makeQuery(id+"F17.opExtrude","CAP_EDGE",EDGE,{"disambiguationData":[OSD([sQuery(id+"F16.wireOp",EDGE,"E57.bottom")])],"isStart":false});
            var Q2;
            Q2=makeQuery(id+"F17.opExtrude","CAP_EDGE",EDGE,{"disambiguationData":[OSD([sQuery(id+"F16.wireOp",EDGE,"E57.right")])],"isStart":false});
            var Q3;
            Q3=makeQuery(id+"F17.opExtrude","CAP_EDGE",EDGE,{"disambiguationData":[OSD([sQuery(id+"F16.wireOp",EDGE,"E57.top")])],"isStart":false});
            chamfer(context, id + "F21", {"entities" : qUnion([Q0, Q1, Q2, Q3]), "width" : 1 * mm, "tangentPropagation" : true});
        }
        {
            var Q0;
            Q0=makeQuery(id+"F1.opExtrude","CAP_FACE",FACE,{"disambiguationData":[OSD([sQuery(id+"F0.wireOp",EDGE,"E0.bottom"),sQuery(id+"F0.wireOp",EDGE,"E0.top"),sQuery(id+"F0.wireOp",EDGE,"E0.left"),sQuery(id+"F0.wireOp",EDGE,"E0.right"),sQuery(id+"F0.wireOp",EDGE,"E1"),sQuery(id+"F0.wireOp",EDGE,"E2"),sQuery(id+"F0.wireOp",EDGE,"E3"),sQuery(id+"F0.wireOp",EDGE,"E4.bottom"),sQuery(id+"F0.wireOp",EDGE,"E4.top"),sQuery(id+"F0.wireOp",EDGE,"E4.left"),sQuery(id+"F0.wireOp",EDGE,"E4.right"),sQuery(id+"F0.wireOp",EDGE,"E11.left"),sQuery(id+"F0.wireOp",EDGE,"E11.right")])],"isStart":false});
            var sketch = newSketch(context, id + "F22", { "sketchPlane" : qUnion([Q0])});
            skCircle(sketch, "E62", {"center": v(-20.5, 23) * mm, "radius": 1.5 * mm});
            skCircle(sketch, "E63", {"center": v(20.5, -23) * mm, "radius": 1.5 * mm});
            skCircle(sketch, "E64", {"center": v(-7.5, -18) * mm, "radius": 8.5 * mm, "construction": true});
            skLineSegment(sketch, "E65.bottom", {"start": v(-25.5, 28) * mm, "end": v(25.5, 28) * mm});
            skLineSegment(sketch, "E65.top", {"start": v(-25.5, -28) * mm, "end": v(25.5, -28) * mm});
            skLineSegment(sketch, "E65.left", {"start": v(-25.5, 28) * mm, "end": v(-25.5, -28) * mm});
            skLineSegment(sketch, "E65.right", {"start": v(25.5, 28) * mm, "end": v(25.5, -28) * mm});
            skLineSegment(sketch, "E66.bottom", {"start": v(-15.25, 11.75) * mm, "end": v(15.25, 11.75) * mm});
            skLineSegment(sketch, "E66.top", {"start": v(-15.25, -2.75) * mm, "end": v(15.25, -2.75) * mm});
            skLineSegment(sketch, "E66.left", {"start": v(-15.25, 11.75) * mm, "end": v(-15.25, -2.75) * mm});
            skLineSegment(sketch, "E66.right", {"start": v(15.25, 11.75) * mm, "end": v(15.25, -2.75) * mm});
            skCircle(sketch, "E67", {"center": v(-22.25, 4.75) * mm, "radius": 2 * mm, "construction": true});
            skCircle(sketch, "E68", {"center": v(22.25, 4.75) * mm, "radius": 2 * mm, "construction": true});
            skLineSegment(sketch, "E69.bottom", {"start": v(5, -27) * mm, "end": v(-20, -27) * mm});
            skLineSegment(sketch, "E69.top", {"start": v(5, -9) * mm, "end": v(-20, -9) * mm});
            skLineSegment(sketch, "E69.left", {"start": v(5, -27) * mm, "end": v(5, -9) * mm});
            skLineSegment(sketch, "E69.right", {"start": v(-20, -27) * mm, "end": v(-20, -9) * mm});
            skSolve(sketch);
        }
        {
            var Q0;
            Q0=makeQuery(id+"F11.opExtrude","CAP_FACE",FACE,{"disambiguationData":[OSD([sQuery(id+"F2.wireOp",EDGE,"E30.bottom"),sQuery(id+"F2.wireOp",EDGE,"E30.top"),sQuery(id+"F2.wireOp",EDGE,"E30.left"),sQuery(id+"F2.wireOp",EDGE,"E30.right"),sQuery(id+"F2.wireOp",EDGE,"E35.bottom"),sQuery(id+"F2.wireOp",EDGE,"E35.top"),sQuery(id+"F2.wireOp",EDGE,"E35.left"),sQuery(id+"F2.wireOp",EDGE,"E35.right"),sQuery(id+"F2.wireOp",EDGE,"E36.left"),sQuery(id+"F2.wireOp",EDGE,"E36.right"),sQuery(id+"F2.wireOp",EDGE,"E37.bottom"),sQuery(id+"F2.wireOp",EDGE,"E37.top")])],"isStart":false});
            var sketch = newSketch(context, id + "F23", { "sketchPlane" : qUnion([Q0])});
            skLineSegment(sketch, "E70.bottom", {"start": v(-63, -101.08) * mm, "end": v(-53, -101.08) * mm});
            skLineSegment(sketch, "E70.top", {"start": v(-63, -102.08) * mm, "end": v(-53, -102.08) * mm});
            skLineSegment(sketch, "E70.left", {"start": v(-63, -101.08) * mm, "end": v(-63, -102.08) * mm});
            skLineSegment(sketch, "E70.right", {"start": v(-53, -101.08) * mm, "end": v(-53, -102.08) * mm});
            skLineSegment(sketch, "E71.bottom", {"start": v(-63, -102.08) * mm, "end": v(-62, -102.08) * mm});
            skLineSegment(sketch, "E71.top", {"start": v(-63, -115.08) * mm, "end": v(-62, -115.08) * mm});
            skLineSegment(sketch, "E71.left", {"start": v(-63, -102.08) * mm, "end": v(-63, -115.08) * mm});
            skLineSegment(sketch, "E71.right", {"start": v(-62, -102.08) * mm, "end": v(-62, -115.08) * mm});
            skLineSegment(sketch, "E72.bottom", {"start": v(-53, -114.08) * mm, "end": v(-62, -114.08) * mm});
            skLineSegment(sketch, "E72.top", {"start": v(-53, -115.08) * mm, "end": v(-62, -115.08) * mm});
            skLineSegment(sketch, "E72.left", {"start": v(-53, -114.08) * mm, "end": v(-53, -115.08) * mm});
            skLineSegment(sketch, "E72.right", {"start": v(-62, -114.08) * mm, "end": v(-62, -115.08) * mm});
            skLineSegment(sketch, "E73.bottom", {"start": v(-33, -101.08) * mm, "end": v(-43, -101.08) * mm});
            skLineSegment(sketch, "E73.top", {"start": v(-33, -102.08) * mm, "end": v(-43, -102.08) * mm});
            skLineSegment(sketch, "E73.left", {"start": v(-33, -101.08) * mm, "end": v(-33, -102.08) * mm});
            skLineSegment(sketch, "E73.right", {"start": v(-43, -101.08) * mm, "end": v(-43, -102.08) * mm});
            skLineSegment(sketch, "E74.bottom", {"start": v(-33, -102.08) * mm, "end": v(-34, -102.08) * mm});
            skLineSegment(sketch, "E74.top", {"start": v(-33, -115.08) * mm, "end": v(-34, -115.08) * mm});
            skLineSegment(sketch, "E74.left", {"start": v(-33, -102.08) * mm, "end": v(-33, -115.08) * mm});
            skLineSegment(sketch, "E74.right", {"start": v(-34, -102.08) * mm, "end": v(-34, -115.08) * mm});
            skLineSegment(sketch, "E75.bottom", {"start": v(-43, -114.08) * mm, "end": v(-34, -114.08) * mm});
            skLineSegment(sketch, "E75.top", {"start": v(-43, -115.08) * mm, "end": v(-34, -115.08) * mm});
            skLineSegment(sketch, "E75.left", {"start": v(-43, -114.08) * mm, "end": v(-43, -115.08) * mm});
            skLineSegment(sketch, "E75.right", {"start": v(-34, -114.08) * mm, "end": v(-34, -115.08) * mm});
            skSolve(sketch);
        }
        {
            var Q0;
            {var subQ0=sQuery(id+"F0.wireOp",EDGE,"E3");Q0=makeQuery(id+"FKRJtqk0ZjomfcX_7.boolean.opBoolean","SPLIT",FACE,{"disambiguationData":[TD([makeQuery(id+"F1.opExtrude","SWEPT_FACE",FACE,{"disambiguationData":[OSD([subQ0])]})])],"derivedFrom":makeQuery(id+"F1.opExtrude","CAP_FACE",FACE,{"disambiguationData":[OSD([sQuery(id+"F0.wireOp",EDGE,"E0.bottom"),sQuery(id+"F0.wireOp",EDGE,"E0.top"),sQuery(id+"F0.wireOp",EDGE,"E0.left"),sQuery(id+"F0.wireOp",EDGE,"E0.right"),sQuery(id+"F0.wireOp",EDGE,"E1"),sQuery(id+"F0.wireOp",EDGE,"E2"),subQ0,sQuery(id+"F0.wireOp",EDGE,"E4.bottom"),sQuery(id+"F0.wireOp",EDGE,"E4.top"),sQuery(id+"F0.wireOp",EDGE,"E4.left"),sQuery(id+"F0.wireOp",EDGE,"E4.right"),sQuery(id+"F0.wireOp",EDGE,"E11.left"),sQuery(id+"F0.wireOp",EDGE,"E11.right")])],"isStart":false})});}
            extrude(context, id + "F24", {"entities" : qUnion([Q0]), "operationType" : NewBodyOperationType.ADD, "depth" : 1 * mm});
        }
        {
            var Q0;
            Q0=sQuery(id+"F22.wireOp",VERTEX,"E67.center");
            var Q1;
            Q1=sQuery(id+"F22.wireOp",VERTEX,"E68.center");
            var Q2;
            Q2=makeQuery(id+"F1.opExtrude","SWEPT_BODY",BODY,{"disambiguationData":[OSD([sQuery(id+"F0.wireOp",EDGE,"E0.bottom"),sQuery(id+"F0.wireOp",EDGE,"E0.top"),sQuery(id+"F0.wireOp",EDGE,"E0.left"),sQuery(id+"F0.wireOp",EDGE,"E0.right"),sQuery(id+"F0.wireOp",EDGE,"E1"),sQuery(id+"F0.wireOp",EDGE,"E2"),sQuery(id+"F0.wireOp",EDGE,"E3"),sQuery(id+"F0.wireOp",EDGE,"E4.bottom"),sQuery(id+"F0.wireOp",EDGE,"E4.top"),sQuery(id+"F0.wireOp",EDGE,"E4.left"),sQuery(id+"F0.wireOp",EDGE,"E4.right"),sQuery(id+"F0.wireOp",EDGE,"E11.left"),sQuery(id+"F0.wireOp",EDGE,"E11.right")])]});
            hole(context, id + "F25", {"style" : HoleStyle.SIMPLE, "endStyle" : HoleEndStyle.THROUGH, "holeDiameter" : 1.4 * mm, "isTappedThrough" : true, "tappedDepth" : 12 * mm, "tapClearance" : 3, "locations" : qUnion([Q0, Q1]), "scope" : qUnion([Q2])});
        }
        {
            var Q0;
            {var subQ0=sQuery(id+"F2.wireOp",EDGE,"E37.top");var subQ1=sQuery(id+"F2.wireOp",EDGE,"E37.bottom");var subQ2=sQuery(id+"F2.wireOp",EDGE,"E36.right");var subQ3=sQuery(id+"F2.wireOp",EDGE,"E36.left");Q0=makeQuery(id+"F13.boolean.opBoolean","MERGE",FACE,{"derivedFrom":[makeQuery(id+"F11.opExtrude","CAP_FACE",FACE,{"disambiguationData":[OSD([sQuery(id+"F2.wireOp",EDGE,"E30.bottom"),sQuery(id+"F2.wireOp",EDGE,"E30.top"),sQuery(id+"F2.wireOp",EDGE,"E30.left"),sQuery(id+"F2.wireOp",EDGE,"E30.right"),sQuery(id+"F2.wireOp",EDGE,"E35.bottom"),sQuery(id+"F2.wireOp",EDGE,"E35.top"),sQuery(id+"F2.wireOp",EDGE,"E35.left"),sQuery(id+"F2.wireOp",EDGE,"E35.right"),subQ3,subQ2,subQ1,subQ0])],"isStart":true}),makeQuery(id+"F13.opExtrude","CAP_FACE",FACE,{"disambiguationData":[OSD([sQuery(id+"F2.wireOp",EDGE,"E36.bottom"),sQuery(id+"F2.wireOp",EDGE,"E36.top"),subQ3,subQ2,subQ1,subQ0,sQuery(id+"F2.wireOp",EDGE,"E37.left"),sQuery(id+"F2.wireOp",EDGE,"E37.right")])],"isStart":true})]});}
            var sketch = newSketch(context, id + "F26", { "sketchPlane" : qUnion([Q0])});
            skLineSegment(sketch, "E76.bottom", {"start": v(-63, 115.08) * mm, "end": v(-33, 115.08) * mm});
            skLineSegment(sketch, "E76.top", {"start": v(-63, 114.08) * mm, "end": v(-33, 114.08) * mm});
            skLineSegment(sketch, "E76.left", {"start": v(-63, 115.08) * mm, "end": v(-63, 114.08) * mm});
            skLineSegment(sketch, "E76.right", {"start": v(-33, 115.08) * mm, "end": v(-33, 114.08) * mm});
            skLineSegment(sketch, "E77.bottom", {"start": v(-63, 114.08) * mm, "end": v(-62, 114.08) * mm});
            skLineSegment(sketch, "E77.top", {"start": v(-63, 101.08) * mm, "end": v(-62, 101.08) * mm});
            skLineSegment(sketch, "E77.left", {"start": v(-63, 114.08) * mm, "end": v(-63, 101.08) * mm});
            skLineSegment(sketch, "E77.right", {"start": v(-62, 114.08) * mm, "end": v(-62, 101.08) * mm});
            skLineSegment(sketch, "E78.bottom", {"start": v(-62, 101.08) * mm, "end": v(-33, 101.08) * mm});
            skLineSegment(sketch, "E78.top", {"start": v(-62, 102.08) * mm, "end": v(-33, 102.08) * mm});
            skLineSegment(sketch, "E78.left", {"start": v(-62, 101.08) * mm, "end": v(-62, 102.08) * mm});
            skLineSegment(sketch, "E78.right", {"start": v(-33, 101.08) * mm, "end": v(-33, 102.08) * mm});
            skLineSegment(sketch, "E79.bottom", {"start": v(-33, 114.08) * mm, "end": v(-34, 114.08) * mm});
            skLineSegment(sketch, "E79.top", {"start": v(-33, 102.08) * mm, "end": v(-34, 102.08) * mm});
            skLineSegment(sketch, "E79.left", {"start": v(-33, 114.08) * mm, "end": v(-33, 102.08) * mm});
            skLineSegment(sketch, "E79.right", {"start": v(-34, 114.08) * mm, "end": v(-34, 102.08) * mm});
            skSolve(sketch);
        }
        {
            var Q0;
            Q0=sQuery(id+"F22.wireOp",VERTEX,"E67.center");
            var Q1;
            Q1=sQuery(id+"F22.wireOp",VERTEX,"E68.center");
            var Q2;
            Q2=makeQuery(id+"F1.opExtrude","SWEPT_BODY",BODY,{"disambiguationData":[OSD([sQuery(id+"F0.wireOp",EDGE,"E0.bottom"),sQuery(id+"F0.wireOp",EDGE,"E0.top"),sQuery(id+"F0.wireOp",EDGE,"E0.left"),sQuery(id+"F0.wireOp",EDGE,"E0.right"),sQuery(id+"F0.wireOp",EDGE,"E1"),sQuery(id+"F0.wireOp",EDGE,"E2"),sQuery(id+"F0.wireOp",EDGE,"E3"),sQuery(id+"F0.wireOp",EDGE,"E4.bottom"),sQuery(id+"F0.wireOp",EDGE,"E4.top"),sQuery(id+"F0.wireOp",EDGE,"E4.left"),sQuery(id+"F0.wireOp",EDGE,"E4.right"),sQuery(id+"F0.wireOp",EDGE,"E11.left"),sQuery(id+"F0.wireOp",EDGE,"E11.right")])]});
            hole(context, id + "F27", {"style" : HoleStyle.SIMPLE, "endStyle" : HoleEndStyle.THROUGH, "oppositeDirection" : true, "holeDiameter" : 1.4 * mm, "isTappedThrough" : true, "tappedDepth" : 12 * mm, "tapClearance" : 3, "locations" : qUnion([Q0, Q1]), "scope" : qUnion([Q2])});
        }
        {
            var Q0;
            Q0=makeQuery(id+"F22.imprint","IMPRINT",FACE,{"disambiguationData":[TD([[makeQuery(id+"F22.imprint","IMPRINT",EDGE,{"derivedFrom":sQuery(id+"F22.wireOp",EDGE,"E62")}),-1.0]])]});
            extrude(context, id + "F28", {"entities" : qUnion([Q0]), "operationType" : NewBodyOperationType.ADD, "depth" : 5 * mm});
        }
        {
            var Q0;
            Q0=makeQuery(id+"F1.opExtrude","CAP_FACE",FACE,{"disambiguationData":[OSD([sQuery(id+"F0.wireOp",EDGE,"E0.bottom"),sQuery(id+"F0.wireOp",EDGE,"E0.top"),sQuery(id+"F0.wireOp",EDGE,"E0.left"),sQuery(id+"F0.wireOp",EDGE,"E0.right"),sQuery(id+"F0.wireOp",EDGE,"E1"),sQuery(id+"F0.wireOp",EDGE,"E2"),sQuery(id+"F0.wireOp",EDGE,"E3"),sQuery(id+"F0.wireOp",EDGE,"E4.bottom"),sQuery(id+"F0.wireOp",EDGE,"E4.top"),sQuery(id+"F0.wireOp",EDGE,"E4.left"),sQuery(id+"F0.wireOp",EDGE,"E4.right"),sQuery(id+"F0.wireOp",EDGE,"E11.left"),sQuery(id+"F0.wireOp",EDGE,"E11.right")])],"isStart":true});
            var sketch = newSketch(context, id + "F29", { "sketchPlane" : qUnion([Q0])});
            skLineSegment(sketch, "E80.bottom", {"start": v(-25.5, 28) * mm, "end": v(25.5, 28) * mm});
            skLineSegment(sketch, "E80.top", {"start": v(-25.5, 27.8) * mm, "end": v(25.5, 27.8) * mm});
            skLineSegment(sketch, "E80.left", {"start": v(-25.5, 28) * mm, "end": v(-25.5, 27.8) * mm});
            skLineSegment(sketch, "E80.right", {"start": v(25.5, 28) * mm, "end": v(25.5, 27.8) * mm});
            skLineSegment(sketch, "E81.bottom", {"start": v(-25.5, -28) * mm, "end": v(25.5, -28) * mm});
            skLineSegment(sketch, "E81.top", {"start": v(-25.5, -27.8) * mm, "end": v(25.5, -27.8) * mm});
            skLineSegment(sketch, "E81.left", {"start": v(-25.5, -28) * mm, "end": v(-25.5, -27.8) * mm});
            skLineSegment(sketch, "E81.right", {"start": v(25.5, -28) * mm, "end": v(25.5, -27.8) * mm});
            skLineSegment(sketch, "E82.bottom", {"start": v(-25.5, -27.8) * mm, "end": v(-25.3, -27.8) * mm});
            skLineSegment(sketch, "E82.top", {"start": v(-25.5, 27.8) * mm, "end": v(-25.3, 27.8) * mm});
            skLineSegment(sketch, "E82.left", {"start": v(-25.5, -27.8) * mm, "end": v(-25.5, 27.8) * mm});
            skLineSegment(sketch, "E82.right", {"start": v(-25.3, -27.8) * mm, "end": v(-25.3, 27.8) * mm});
            skLineSegment(sketch, "E83.bottom", {"start": v(25.5, -27.8) * mm, "end": v(25.3, -27.8) * mm});
            skLineSegment(sketch, "E83.top", {"start": v(25.5, 27.8) * mm, "end": v(25.3, 27.8) * mm});
            skLineSegment(sketch, "E83.left", {"start": v(25.5, -27.8) * mm, "end": v(25.5, 27.8) * mm});
            skLineSegment(sketch, "E83.right", {"start": v(25.3, -27.8) * mm, "end": v(25.3, 27.8) * mm});
            skSolve(sketch);
        }
        {
            var Q0;
            Q0 = qSketchRegion(id + "F29", true);
            extrude(context, id + "F30", {"entities" : qUnion([Q0]), "operationType" : NewBodyOperationType.REMOVE, "oppositeDirection" : true, "depth" : 25 * mm});
        }
        {
            var Q0;
            Q0=sQuery(id+"F22.wireOp",VERTEX,"E67.center");
            var Q1;
            Q1=sQuery(id+"F22.wireOp",VERTEX,"E68.center");
            var Q2;
            Q2=makeQuery(id+"F1.opExtrude","SWEPT_BODY",BODY,{"disambiguationData":[OSD([sQuery(id+"F0.wireOp",EDGE,"E0.bottom"),sQuery(id+"F0.wireOp",EDGE,"E0.top"),sQuery(id+"F0.wireOp",EDGE,"E0.left"),sQuery(id+"F0.wireOp",EDGE,"E0.right"),sQuery(id+"F0.wireOp",EDGE,"E1"),sQuery(id+"F0.wireOp",EDGE,"E2"),sQuery(id+"F0.wireOp",EDGE,"E3"),sQuery(id+"F0.wireOp",EDGE,"E4.bottom"),sQuery(id+"F0.wireOp",EDGE,"E4.top"),sQuery(id+"F0.wireOp",EDGE,"E4.left"),sQuery(id+"F0.wireOp",EDGE,"E4.right"),sQuery(id+"F0.wireOp",EDGE,"E11.left"),sQuery(id+"F0.wireOp",EDGE,"E11.right")])]});
            hole(context, id + "F31", {"style" : HoleStyle.SIMPLE, "endStyle" : HoleEndStyle.THROUGH, "oppositeDirection" : true, "holeDiameter" : 1.6 * mm, "isTappedThrough" : true, "tappedDepth" : 12 * mm, "tapClearance" : 3, "locations" : qUnion([Q0, Q1]), "scope" : qUnion([Q2])});
        }
        {
            var Q0;
            Q0=sQuery(id+"F22.wireOp",VERTEX,"E68.center");
            var Q1;
            Q1=sQuery(id+"F22.wireOp",VERTEX,"E67.center");
            var Q2;
            Q2=makeQuery(id+"F1.opExtrude","SWEPT_BODY",BODY,{"disambiguationData":[OSD([sQuery(id+"F0.wireOp",EDGE,"E0.bottom"),sQuery(id+"F0.wireOp",EDGE,"E0.top"),sQuery(id+"F0.wireOp",EDGE,"E0.left"),sQuery(id+"F0.wireOp",EDGE,"E0.right"),sQuery(id+"F0.wireOp",EDGE,"E1"),sQuery(id+"F0.wireOp",EDGE,"E2"),sQuery(id+"F0.wireOp",EDGE,"E3"),sQuery(id+"F0.wireOp",EDGE,"E4.bottom"),sQuery(id+"F0.wireOp",EDGE,"E4.top"),sQuery(id+"F0.wireOp",EDGE,"E4.left"),sQuery(id+"F0.wireOp",EDGE,"E4.right"),sQuery(id+"F0.wireOp",EDGE,"E11.left"),sQuery(id+"F0.wireOp",EDGE,"E11.right")])]});
            hole(context, id + "F32", {"style" : HoleStyle.SIMPLE, "endStyle" : HoleEndStyle.THROUGH, "holeDiameter" : 1.6 * mm, "isTappedThrough" : true, "tappedDepth" : 12 * mm, "tapClearance" : 3, "locations" : qUnion([Q0, Q1]), "scope" : qUnion([Q2])});
        }
    });
